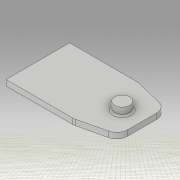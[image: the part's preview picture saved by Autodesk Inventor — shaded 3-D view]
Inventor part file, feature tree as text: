
AUTODESK INVENTOR PART (.ipt)
format: ipt  version: 2018 (Build 220112000, 112)  size: 124,416 bytes
history: native  units: in
note: dims shown in document units (in); Inventor stores cm internally (conversion verified against a paired STEP export)
features: extrude x2, fillet x2, sketch x2
ambient origin geometry x8: Origin, YZ Plane, XZ Plane, XY Plane, X Axis, Y Axis, Z Axis, Center Point
bodies: Solid1 (feature_tree)
feature tree (6):
  extrude  "Extrusion1"  Depth=0.727in
  extrude  "Extrusion2"  Depth=0.125in
  fillet  "Fillet1"  Radius=0.415in
  fillet  "Fillet2"  Radius=0.065in
  sketch  "Sketch1"  dims[d0=1.193in d1=0.727in]
  sketch  "Sketch2"  dims[d2=0.265in d3=0.53in d4=0.415in d5=0.065in d6=0.0in d7=0.17in d8=0.36in d9=0.225in d10=0.09in d11=0.0in d12=0.02in d13=0.125in]
